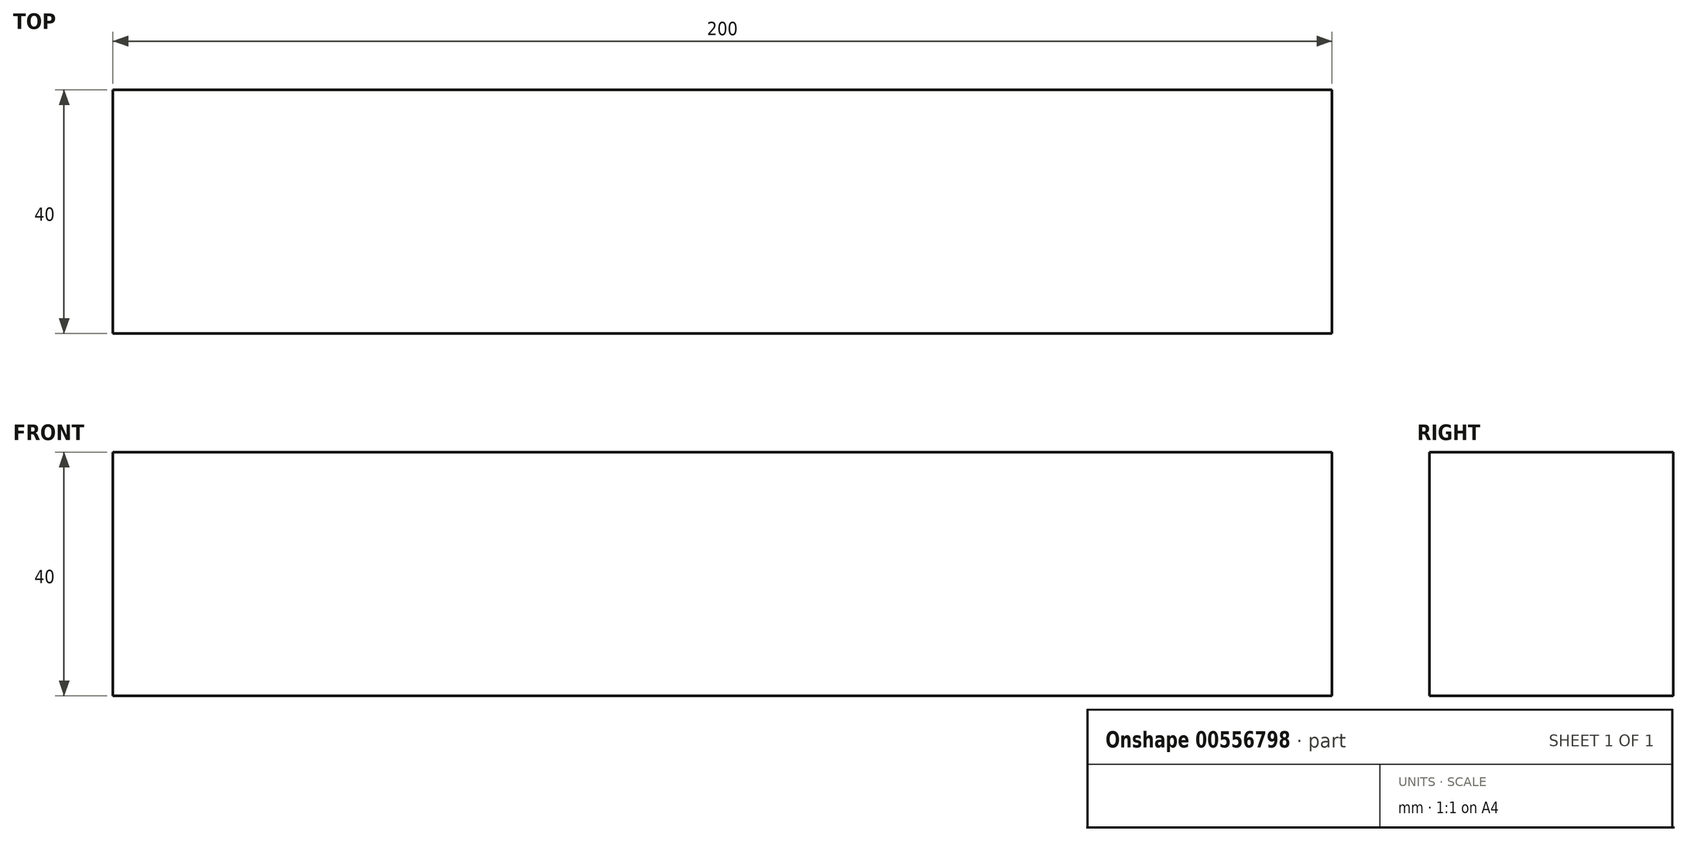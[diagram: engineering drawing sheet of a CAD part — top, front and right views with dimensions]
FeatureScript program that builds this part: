
annotation { "Feature Type Name" : "Feature", "Feature Type Description" : "" }
export const myFeature = defineFeature(function(context is Context, id is Id, definition is map)
    precondition{}
    {
        {
            var Q0;
            Q0=qCreatedBy(makeId("Front.planeOp"),FACE);
            var sketch = newSketch(context, id + "F0", { "sketchPlane" : qUnion([Q0])});
            skLineSegment(sketch, "E0.bottom", {"start": v(-100, 20) * mm, "end": v(100, 20) * mm});
            skLineSegment(sketch, "E0.top", {"start": v(-100, -20) * mm, "end": v(100, -20) * mm});
            skLineSegment(sketch, "E0.left", {"start": v(-100, 20) * mm, "end": v(-100, -20) * mm});
            skLineSegment(sketch, "E0.right", {"start": v(100, 20) * mm, "end": v(100, -20) * mm});
            skPoint(sketch, "E0.middle", {"position": v(0, 0) * mm});
            skSolve(sketch);
        }
        {
            var Q0;
            Q0=qSketchRegion(id+"F0",true);
            extrude(context, id + "F1", {"entities" : qUnion([Q0]), "depth" : 40 * mm, "offsetDistance" : 25 * mm});
        }
    });
